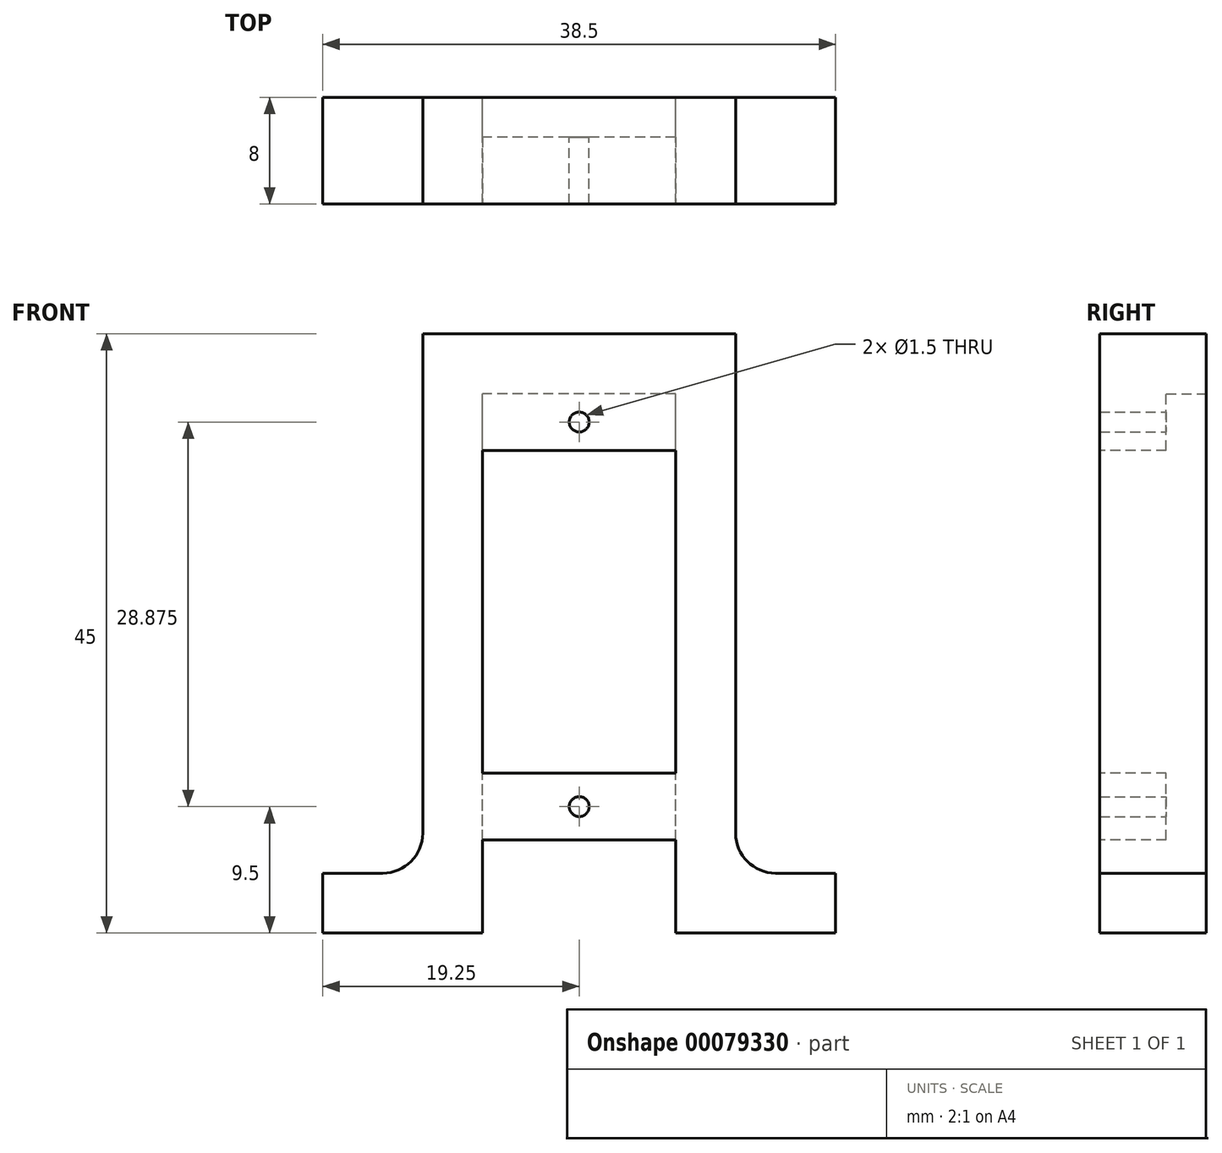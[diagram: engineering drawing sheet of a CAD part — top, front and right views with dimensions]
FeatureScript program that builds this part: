
annotation { "Feature Type Name" : "Feature", "Feature Type Description" : "" }
export const myFeature = defineFeature(function(context is Context, id is Id, definition is map)
    precondition{}
    {
        {
            var Q0;
            Q0=qCreatedBy(makeId("Front.planeOp"),FACE);
            var sketch = newSketch(context, id + "F0", { "sketchPlane" : qUnion([Q0])});
            skLineSegment(sketch, "E0", {"start": v(-19.25, 0) * mm, "end": v(-19.25, 4.5) * mm});
            skLineSegment(sketch, "E1", {"start": v(-19.25, 4.5) * mm, "end": v(-14.75, 4.5) * mm});
            skLineSegment(sketch, "E2", {"start": v(-11.75, 7.5) * mm, "end": v(-11.75, 45) * mm});
            skLineSegment(sketch, "E3", {"start": v(-11.75, 45) * mm, "end": v(11.75, 45) * mm});
            skLineSegment(sketch, "E4", {"start": v(11.75, 45) * mm, "end": v(11.75, 7.5) * mm});
            skLineSegment(sketch, "E5", {"start": v(14.75, 4.5) * mm, "end": v(19.25, 4.5) * mm});
            skLineSegment(sketch, "E6", {"start": v(19.25, 4.5) * mm, "end": v(19.25, 0) * mm});
            skLineSegment(sketch, "E7", {"start": v(19.25, 0) * mm, "end": v(7.25, 0) * mm});
            skLineSegment(sketch, "E8", {"start": v(7.25, 0) * mm, "end": v(7.25, 40.5) * mm});
            skLineSegment(sketch, "E9", {"start": v(7.25, 40.5) * mm, "end": v(-7.25, 40.5) * mm});
            skLineSegment(sketch, "E10", {"start": v(-7.25, 0) * mm, "end": v(-19.25, 0) * mm});
            skLineSegment(sketch, "E11", {"start": v(-7.25, 0) * mm, "end": v(-7.25, 40.5) * mm});
            skPoint(sketch, "E12.visualSharp", {"position": v(-11.75, 4.5) * mm});
            skArc(sketch, "E12.filletArc", {"start": v(-14.75, 4.5) * mm, "mid": v(-12.63, 5.38) * mm, "end": v(-11.75, 7.5) * mm});
            skPoint(sketch, "E13.visualSharp", {"position": v(11.75, 4.5) * mm});
            skArc(sketch, "E13.filletArc", {"start": v(11.75, 7.5) * mm, "mid": v(12.63, 5.38) * mm, "end": v(14.75, 4.5) * mm});
            skSolve(sketch);
        }
        {
            var Q0;
            Q0 = qSketchRegion(id + "F0", true);
            extrude(context, id + "F1", {"entities" : qUnion([Q0]), "depth" : 8 * mm});
        }
        {
            var Q0;
            Q0=makeQuery(id+"F1.opExtrude","CAP_FACE",FACE,{"disambiguationData":[OSD([sQuery(id+"F0.wireOp",EDGE,"E0"),sQuery(id+"F0.wireOp",EDGE,"E1"),sQuery(id+"F0.wireOp",EDGE,"E2"),sQuery(id+"F0.wireOp",EDGE,"E3"),sQuery(id+"F0.wireOp",EDGE,"E4"),sQuery(id+"F0.wireOp",EDGE,"E5"),sQuery(id+"F0.wireOp",EDGE,"E6"),sQuery(id+"F0.wireOp",EDGE,"E7"),sQuery(id+"F0.wireOp",EDGE,"E8"),sQuery(id+"F0.wireOp",EDGE,"E9"),sQuery(id+"F0.wireOp",EDGE,"E10"),sQuery(id+"F0.wireOp",EDGE,"E11"),sQuery(id+"F0.wireOp",EDGE,"E12.filletArc"),sQuery(id+"F0.wireOp",EDGE,"E13.filletArc")])],"isStart":false});
            var sketch = newSketch(context, id + "F2", { "sketchPlane" : qUnion([Q0])});
            skLineSegment(sketch, "E14.bottom", {"start": v(-7.25, 40.5) * mm, "end": v(7.25, 40.5) * mm});
            skLineSegment(sketch, "E14.top", {"start": v(-7.25, 36.25) * mm, "end": v(7.25, 36.25) * mm});
            skLineSegment(sketch, "E14.left", {"start": v(-7.25, 40.5) * mm, "end": v(-7.25, 36.25) * mm});
            skLineSegment(sketch, "E14.right", {"start": v(7.25, 40.5) * mm, "end": v(7.25, 36.25) * mm});
            skLineSegment(sketch, "E15.bottom", {"start": v(-7.25, 12) * mm, "end": v(7.25, 12) * mm});
            skLineSegment(sketch, "E15.top", {"start": v(-7.25, 7) * mm, "end": v(7.25, 7) * mm});
            skLineSegment(sketch, "E15.left", {"start": v(-7.25, 12) * mm, "end": v(-7.25, 7) * mm});
            skLineSegment(sketch, "E15.right", {"start": v(7.25, 12) * mm, "end": v(7.25, 7) * mm});
            skSolve(sketch);
        }
        {
            var Q0;
            Q0 = qSketchRegion(id + "F2", true);
            extrude(context, id + "F3", {"entities" : qUnion([Q0]), "operationType" : NewBodyOperationType.ADD, "oppositeDirection" : true, "depth" : 5 * mm});
        }
        {
            var Q0;
            Q0=makeQuery(id+"F3.opExtrude","CAP_FACE",FACE,{"disambiguationData":[OSD([sQuery(id+"F2.wireOp",EDGE,"E14.bottom"),sQuery(id+"F2.wireOp",EDGE,"E14.top"),sQuery(id+"F2.wireOp",EDGE,"E14.left"),sQuery(id+"F2.wireOp",EDGE,"E14.right")])],"isStart":false});
            var sketch = newSketch(context, id + "F4", { "sketchPlane" : qUnion([Q0])});
            skCircle(sketch, "E16", {"center": v(0, 38.38) * mm, "radius": 0.75 * mm});
            skCircle(sketch, "E17", {"center": v(0, 9.5) * mm, "radius": 0.75 * mm});
            skLineSegment(sketch, "E18", {"start": v(0, 7) * mm, "end": v(0, 12) * mm, "construction": true});
            skLineSegment(sketch, "E19", {"start": v(0, 40.5) * mm, "end": v(0, 36.25) * mm, "construction": true});
            skPoint(sketch, "E19.endSnap0", {"position": v(0, 36.25) * mm});
            skSolve(sketch);
        }
        {
            var Q0;
            Q0 = qSketchRegion(id + "F4", true);
            extrude(context, id + "F5", {"entities" : qUnion([Q0]), "operationType" : NewBodyOperationType.REMOVE, "endBound" : BoundingType.THROUGH_ALL, "oppositeDirection" : true, "depth" : 25 * mm});
        }
    });
